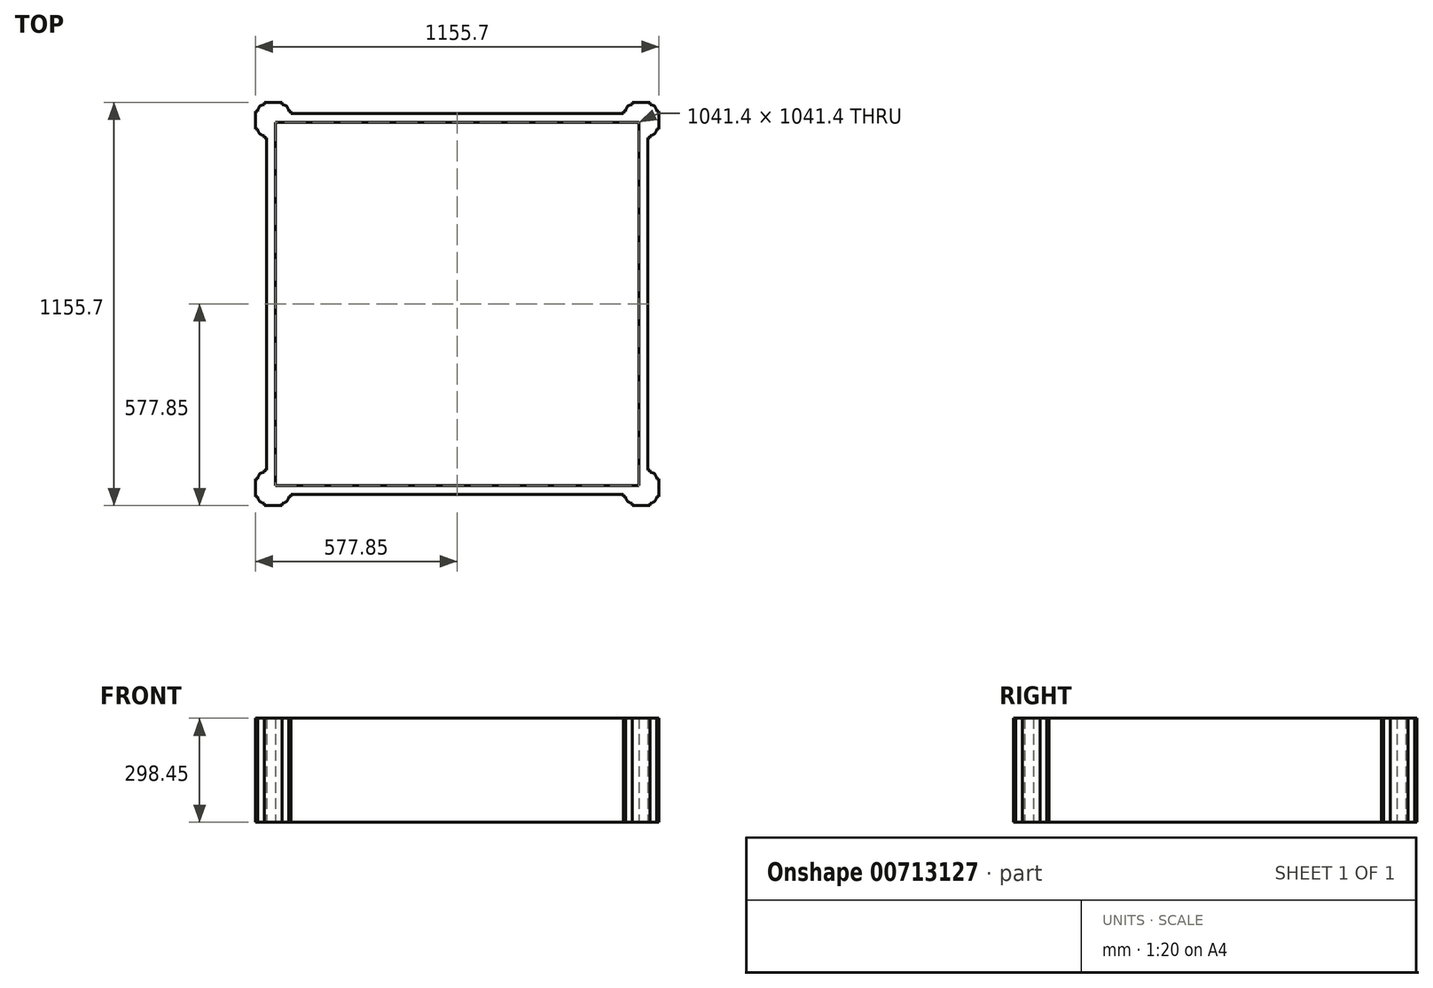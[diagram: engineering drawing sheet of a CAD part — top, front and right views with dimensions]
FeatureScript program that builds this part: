
annotation { "Feature Type Name" : "Feature", "Feature Type Description" : "" }
export const myFeature = defineFeature(function(context is Context, id is Id, definition is map)
    precondition{}
    {
        {
            var Q0;
            Q0=qCreatedBy(makeId("Top.planeOp"),FACE);
            var sketch = newSketch(context, id + "F0", { "sketchPlane" : qUnion([Q0])});
            skLineSegment(sketch, "E0.bottom", {"start": v(-546.1, 476.25) * mm, "end": v(-552.45, 476.25) * mm});
            skLineSegment(sketch, "E0.top", {"start": v(-501.65, 577.85) * mm, "end": v(-552.45, 577.85) * mm});
            skLineSegment(sketch, "E0.left", {"start": v(-476.25, 546.1) * mm, "end": v(-476.25, 552.45) * mm});
            skLineSegment(sketch, "E0.right", {"start": v(-577.85, 501.65) * mm, "end": v(-577.85, 552.45) * mm});
            skLineSegment(sketch, "E1", {"start": v(-552.45, 577.85) * mm, "end": v(-552.45, 571.5) * mm});
            skLineSegment(sketch, "E2.MirrorCS", {"start": v(-577.85, 552.45) * mm, "end": v(-571.5, 552.45) * mm});
            skArc(sketch, "E3", {"start": v(-552.45, 571.5) * mm, "mid": v(-565.92, 565.92) * mm, "end": v(-571.5, 552.45) * mm});
            skLineSegment(sketch, "E4.MirrorCS", {"start": v(-501.65, 577.85) * mm, "end": v(-501.65, 571.5) * mm});
            skLineSegment(sketch, "E5.MirrorCS", {"start": v(-476.25, 552.45) * mm, "end": v(-482.6, 552.45) * mm});
            skArc(sketch, "E6.MirrorCS", {"start": v(-501.65, 571.5) * mm, "mid": v(-488.18, 565.92) * mm, "end": v(-482.6, 552.45) * mm});
            skLineSegment(sketch, "E7.MirrorCS", {"start": v(-552.45, 577.85) * mm, "end": v(-501.65, 577.85) * mm});
            skLineSegment(sketch, "E8.MirrorCS", {"start": v(-577.85, 501.65) * mm, "end": v(-571.5, 501.65) * mm});
            skLineSegment(sketch, "E9.MirrorCS", {"start": v(-552.45, 476.25) * mm, "end": v(-552.45, 482.6) * mm});
            skArc(sketch, "E10.MirrorCS", {"start": v(-552.45, 482.6) * mm, "mid": v(-565.92, 488.18) * mm, "end": v(-571.5, 501.65) * mm});
            skLineSegment(sketch, "E11.MirrorCS", {"start": v(-552.45, 476.25) * mm, "end": v(-546.1, 476.25) * mm});
            skLineSegment(sketch, "E12.bottom", {"start": v(476.25, -546.1) * mm, "end": v(-476.25, -546.1) * mm});
            skLineSegment(sketch, "E12.top", {"start": v(476.25, 546.1) * mm, "end": v(-476.25, 546.1) * mm});
            skLineSegment(sketch, "E12.left", {"start": v(546.1, -476.25) * mm, "end": v(546.1, 476.25) * mm});
            skLineSegment(sketch, "E12.right", {"start": v(-546.1, -476.25) * mm, "end": v(-546.1, 476.25) * mm});
            skPoint(sketch, "E12.middle", {"position": v(0, 0) * mm});
            skLineSegment(sketch, "E13", {"start": v(0, 0) * mm, "end": v(0, 604.97) * mm, "construction": true});
            skLineSegment(sketch, "E14", {"start": v(0, 0) * mm, "end": v(734.39, 0) * mm, "construction": true});
            skLineSegment(sketch, "E15.MirrorCS", {"start": v(546.1, 476.25) * mm, "end": v(552.45, 476.25) * mm});
            skLineSegment(sketch, "E16.MirrorCS", {"start": v(552.45, 476.25) * mm, "end": v(552.45, 482.6) * mm});
            skLineSegment(sketch, "E17.MirrorCS", {"start": v(552.45, 577.85) * mm, "end": v(552.45, 571.5) * mm});
            skArc(sketch, "E18.MirrorCS", {"start": v(552.45, 571.5) * mm, "mid": v(565.92, 565.92) * mm, "end": v(571.5, 552.45) * mm});
            skArc(sketch, "E19.MirrorCS", {"start": v(552.45, 482.6) * mm, "mid": v(565.92, 488.18) * mm, "end": v(571.5, 501.65) * mm});
            skLineSegment(sketch, "E20.MirrorCS", {"start": v(552.45, 476.25) * mm, "end": v(546.1, 476.25) * mm});
            skLineSegment(sketch, "E21.MirrorCS", {"start": v(476.25, 552.45) * mm, "end": v(482.6, 552.45) * mm});
            skLineSegment(sketch, "E22.MirrorCS", {"start": v(577.85, 501.65) * mm, "end": v(571.5, 501.65) * mm});
            skArc(sketch, "E23.MirrorCS", {"start": v(501.65, 571.5) * mm, "mid": v(488.18, 565.92) * mm, "end": v(482.6, 552.45) * mm});
            skLineSegment(sketch, "E24.MirrorCS", {"start": v(501.65, 577.85) * mm, "end": v(501.65, 571.5) * mm});
            skLineSegment(sketch, "E25.MirrorCS", {"start": v(577.85, 552.45) * mm, "end": v(571.5, 552.45) * mm});
            skLineSegment(sketch, "E26.MirrorCS", {"start": v(476.25, 546.1) * mm, "end": v(476.25, 552.45) * mm});
            skLineSegment(sketch, "E27.MirrorCS", {"start": v(552.45, 577.85) * mm, "end": v(501.65, 577.85) * mm});
            skLineSegment(sketch, "E28.MirrorCS", {"start": v(577.85, 501.65) * mm, "end": v(577.85, 552.45) * mm});
            skLineSegment(sketch, "E29.MirrorCS", {"start": v(501.65, 577.85) * mm, "end": v(552.45, 577.85) * mm});
            skLineSegment(sketch, "E30.MirrorCS", {"start": v(-546.1, -476.25) * mm, "end": v(-552.45, -476.25) * mm});
            skLineSegment(sketch, "E31.MirrorCS", {"start": v(546.1, -476.25) * mm, "end": v(552.45, -476.25) * mm});
            skLineSegment(sketch, "E32.MirrorCS", {"start": v(-552.45, -476.25) * mm, "end": v(-552.45, -482.6) * mm});
            skLineSegment(sketch, "E33.MirrorCS", {"start": v(552.45, -476.25) * mm, "end": v(552.45, -482.6) * mm});
            skLineSegment(sketch, "E34.MirrorCS", {"start": v(552.45, -476.25) * mm, "end": v(546.1, -476.25) * mm});
            skLineSegment(sketch, "E35.MirrorCS", {"start": v(-552.45, -476.25) * mm, "end": v(-546.1, -476.25) * mm});
            skLineSegment(sketch, "E36.MirrorCS", {"start": v(-552.45, -577.85) * mm, "end": v(-552.45, -571.5) * mm});
            skArc(sketch, "E37.MirrorCS", {"start": v(-552.45, -571.5) * mm, "mid": v(-565.92, -565.92) * mm, "end": v(-571.5, -552.45) * mm});
            skArc(sketch, "E38.MirrorCS", {"start": v(-501.65, -571.5) * mm, "mid": v(-488.18, -565.92) * mm, "end": v(-482.6, -552.45) * mm});
            skLineSegment(sketch, "E39.MirrorCS", {"start": v(-476.25, -552.45) * mm, "end": v(-482.6, -552.45) * mm});
            skLineSegment(sketch, "E40.MirrorCS", {"start": v(501.65, -577.85) * mm, "end": v(501.65, -571.5) * mm});
            skLineSegment(sketch, "E41.MirrorCS", {"start": v(476.25, -552.45) * mm, "end": v(482.6, -552.45) * mm});
            skLineSegment(sketch, "E42.MirrorCS", {"start": v(552.45, -577.85) * mm, "end": v(552.45, -571.5) * mm});
            skLineSegment(sketch, "E43.MirrorCS", {"start": v(577.85, -501.65) * mm, "end": v(571.5, -501.65) * mm});
            skArc(sketch, "E44.MirrorCS", {"start": v(-552.45, -482.6) * mm, "mid": v(-565.92, -488.18) * mm, "end": v(-571.5, -501.65) * mm});
            skLineSegment(sketch, "E45.MirrorCS", {"start": v(577.85, -552.45) * mm, "end": v(571.5, -552.45) * mm});
            skLineSegment(sketch, "E46.MirrorCS", {"start": v(-577.85, -552.45) * mm, "end": v(-571.5, -552.45) * mm});
            skLineSegment(sketch, "E47.MirrorCS", {"start": v(-476.25, -546.1) * mm, "end": v(-476.25, -552.45) * mm});
            skArc(sketch, "E48.MirrorCS", {"start": v(501.65, -571.5) * mm, "mid": v(488.18, -565.92) * mm, "end": v(482.6, -552.45) * mm});
            skLineSegment(sketch, "E49.MirrorCS", {"start": v(-501.65, -577.85) * mm, "end": v(-501.65, -571.5) * mm});
            skLineSegment(sketch, "E50.MirrorCS", {"start": v(-577.85, -501.65) * mm, "end": v(-571.5, -501.65) * mm});
            skArc(sketch, "E51.MirrorCS", {"start": v(552.45, -482.6) * mm, "mid": v(565.92, -488.18) * mm, "end": v(571.5, -501.65) * mm});
            skArc(sketch, "E52.MirrorCS", {"start": v(552.45, -571.5) * mm, "mid": v(565.92, -565.92) * mm, "end": v(571.5, -552.45) * mm});
            skLineSegment(sketch, "E53.MirrorCS", {"start": v(476.25, -546.1) * mm, "end": v(476.25, -552.45) * mm});
            skLineSegment(sketch, "E54.MirrorCS", {"start": v(-552.45, -577.85) * mm, "end": v(-501.65, -577.85) * mm});
            skLineSegment(sketch, "E55.MirrorCS", {"start": v(501.65, -577.85) * mm, "end": v(552.45, -577.85) * mm});
            skLineSegment(sketch, "E56.MirrorCS", {"start": v(-501.65, -577.85) * mm, "end": v(-552.45, -577.85) * mm});
            skLineSegment(sketch, "E57.MirrorCS", {"start": v(577.85, -501.65) * mm, "end": v(577.85, -552.45) * mm});
            skPoint(sketch, "E58.MirrorP", {"position": v(-527.05, -527.05) * mm});
            skPoint(sketch, "E59.MirrorP", {"position": v(577.85, -577.85) * mm});
            skLineSegment(sketch, "E60.MirrorCS", {"start": v(552.45, -577.85) * mm, "end": v(501.65, -577.85) * mm});
            skLineSegment(sketch, "E61.MirrorCS", {"start": v(-577.85, -501.65) * mm, "end": v(-577.85, -552.45) * mm});
            skSolve(sketch);
        }
        {
            var Q0;
            Q0=makeQuery(id+"F0.imprint","IMPRINT",FACE,{"disambiguationData":[TD([[makeQuery(id+"F0.imprint","IMPRINT",EDGE,{"derivedFrom":sQuery(id+"F0.wireOp",EDGE,"E0.left")}),1.0]])]});
            extrude(context, id + "F1", {"entities" : qUnion([Q0]), "depth" : 298.45 * mm, "offsetDistance" : 25.4 * mm});
        }
        {
            var Q0;
            Q0=makeQuery(id+"F1.opExtrude","CAP_FACE",FACE,{"disambiguationData":[OSD([sQuery(id+"F0.wireOp",EDGE,"E0.left"),sQuery(id+"F0.wireOp",EDGE,"E0.right"),sQuery(id+"F0.wireOp",EDGE,"E4.MirrorCS"),sQuery(id+"F0.wireOp",EDGE,"E5.MirrorCS"),sQuery(id+"F0.wireOp",EDGE,"E2.MirrorCS"),sQuery(id+"F0.wireOp",EDGE,"E1"),sQuery(id+"F0.wireOp",EDGE,"E7.MirrorCS"),sQuery(id+"F0.wireOp",EDGE,"E3"),sQuery(id+"F0.wireOp",EDGE,"E6.MirrorCS"),sQuery(id+"F0.wireOp",EDGE,"E9.MirrorCS"),sQuery(id+"F0.wireOp",EDGE,"E8.MirrorCS"),sQuery(id+"F0.wireOp",EDGE,"E0.bottom"),sQuery(id+"F0.wireOp",EDGE,"E10.MirrorCS"),sQuery(id+"F0.wireOp",EDGE,"E12.bottom"),sQuery(id+"F0.wireOp",EDGE,"E12.top"),sQuery(id+"F0.wireOp",EDGE,"E12.left"),sQuery(id+"F0.wireOp",EDGE,"E12.right"),sQuery(id+"F0.wireOp",EDGE,"E16.MirrorCS"),sQuery(id+"F0.wireOp",EDGE,"E20.MirrorCS"),sQuery(id+"F0.wireOp",EDGE,"E19.MirrorCS"),sQuery(id+"F0.wireOp",EDGE,"E18.MirrorCS"),sQuery(id+"F0.wireOp",EDGE,"E21.MirrorCS"),sQuery(id+"F0.wireOp",EDGE,"E17.MirrorCS"),sQuery(id+"F0.wireOp",EDGE,"E26.MirrorCS"),sQuery(id+"F0.wireOp",EDGE,"E22.MirrorCS"),sQuery(id+"F0.wireOp",EDGE,"E23.MirrorCS"),sQuery(id+"F0.wireOp",EDGE,"E25.MirrorCS"),sQuery(id+"F0.wireOp",EDGE,"E24.MirrorCS"),sQuery(id+"F0.wireOp",EDGE,"E28.MirrorCS"),sQuery(id+"F0.wireOp",EDGE,"E29.MirrorCS"),sQuery(id+"F0.wireOp",EDGE,"E32.MirrorCS"),sQuery(id+"F0.wireOp",EDGE,"E35.MirrorCS"),sQuery(id+"F0.wireOp",EDGE,"E33.MirrorCS"),sQuery(id+"F0.wireOp",EDGE,"E31.MirrorCS"),sQuery(id+"F0.wireOp",EDGE,"E38.MirrorCS"),sQuery(id+"F0.wireOp",EDGE,"E47.MirrorCS"),sQuery(id+"F0.wireOp",EDGE,"E36.MirrorCS"),sQuery(id+"F0.wireOp",EDGE,"E37.MirrorCS"),sQuery(id+"F0.wireOp",EDGE,"E39.MirrorCS"),sQuery(id+"F0.wireOp",EDGE,"E41.MirrorCS"),sQuery(id+"F0.wireOp",EDGE,"E40.MirrorCS"),sQuery(id+"F0.wireOp",EDGE,"E42.MirrorCS"),sQuery(id+"F0.wireOp",EDGE,"E48.MirrorCS"),sQuery(id+"F0.wireOp",EDGE,"E43.MirrorCS"),sQuery(id+"F0.wireOp",EDGE,"E50.MirrorCS"),sQuery(id+"F0.wireOp",EDGE,"E44.MirrorCS"),sQuery(id+"F0.wireOp",EDGE,"E51.MirrorCS"),sQuery(id+"F0.wireOp",EDGE,"E45.MirrorCS"),sQuery(id+"F0.wireOp",EDGE,"E53.MirrorCS"),sQuery(id+"F0.wireOp",EDGE,"E52.MirrorCS"),sQuery(id+"F0.wireOp",EDGE,"E49.MirrorCS"),sQuery(id+"F0.wireOp",EDGE,"E46.MirrorCS"),sQuery(id+"F0.wireOp",EDGE,"E56.MirrorCS"),sQuery(id+"F0.wireOp",EDGE,"E57.MirrorCS"),sQuery(id+"F0.wireOp",EDGE,"E60.MirrorCS"),sQuery(id+"F0.wireOp",EDGE,"E61.MirrorCS")])],"isStart":true});
            var sketch = newSketch(context, id + "F2", { "sketchPlane" : qUnion([Q0])});
            skLineSegment(sketch, "E62.bottom", {"start": v(520.7, -520.7) * mm, "end": v(-520.7, -520.7) * mm});
            skLineSegment(sketch, "E62.top", {"start": v(520.7, 520.7) * mm, "end": v(-520.7, 520.7) * mm});
            skLineSegment(sketch, "E62.left", {"start": v(520.7, -520.7) * mm, "end": v(520.7, 520.7) * mm});
            skLineSegment(sketch, "E62.right", {"start": v(-520.7, -520.7) * mm, "end": v(-520.7, 520.7) * mm});
            skPoint(sketch, "E62.middle", {"position": v(0, 0) * mm});
            skSolve(sketch);
        }
        {
            var Q0;
            Q0=makeQuery(id+"F2.imprint","IMPRINT",FACE,{"disambiguationData":[TD([[makeQuery(id+"F2.imprint","IMPRINT",EDGE,{"derivedFrom":sQuery(id+"F2.wireOp",EDGE,"E62.bottom")}),-1.0]])]});
            extrude(context, id + "F3", {"entities" : qUnion([Q0]), "operationType" : NewBodyOperationType.REMOVE, "endBound" : BoundingType.THROUGH_ALL, "oppositeDirection" : true, "depth" : 25.4 * mm, "offsetDistance" : 25.4 * mm});
        }
    });
